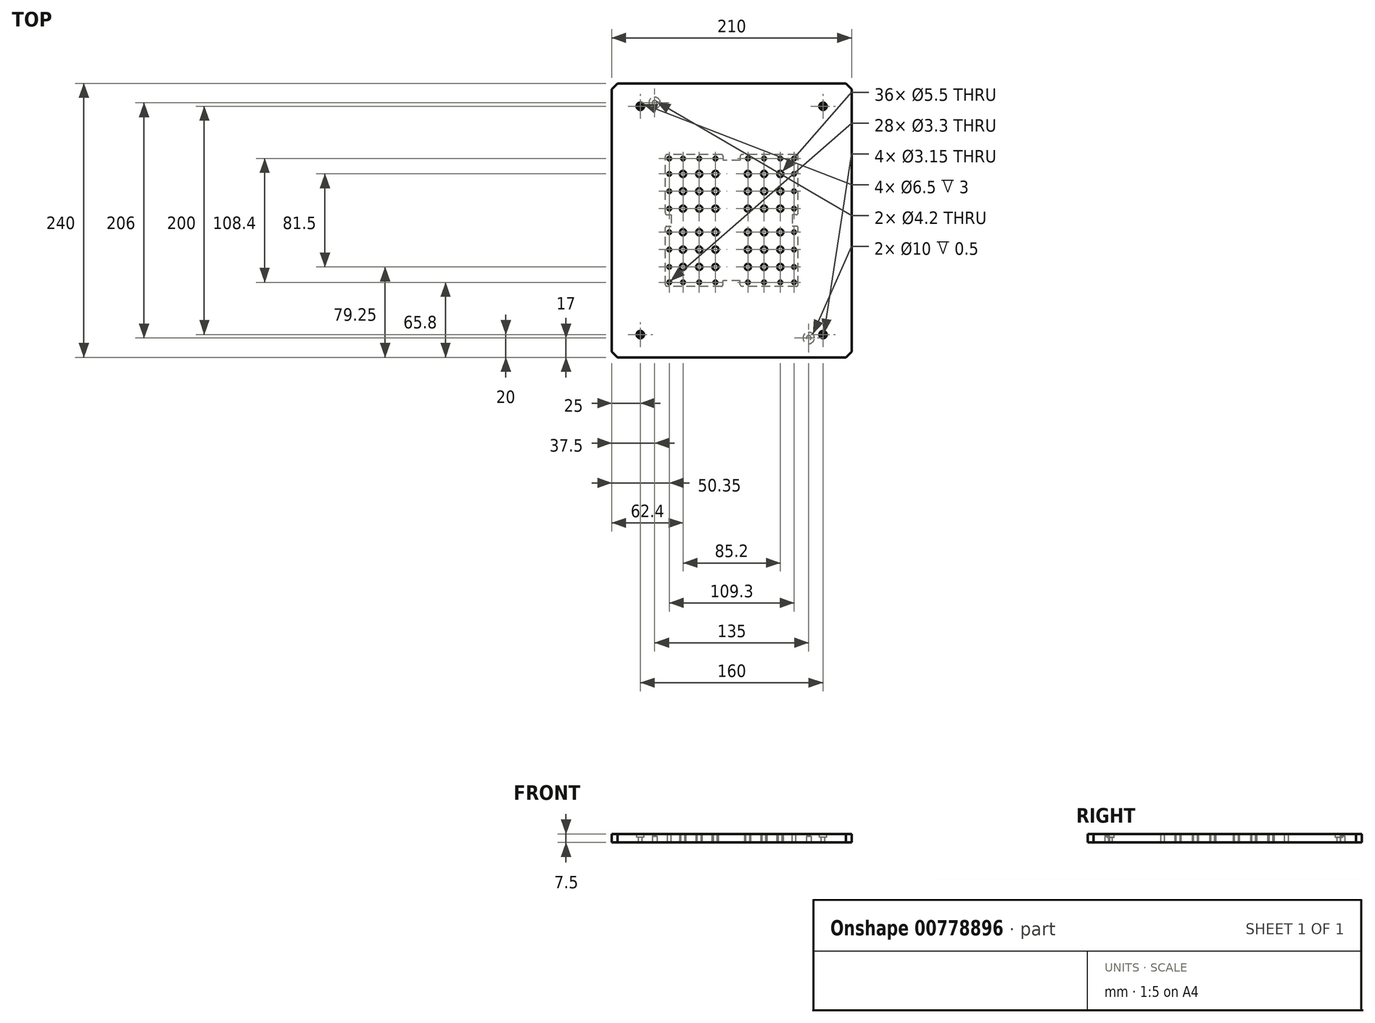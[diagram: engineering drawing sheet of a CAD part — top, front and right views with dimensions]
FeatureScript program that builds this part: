
annotation { "Feature Type Name" : "Feature", "Feature Type Description" : "" }
export const myFeature = defineFeature(function(context is Context, id is Id, definition is map)
    precondition{}
    {
        {
            var Q0;
            Q0=qCreatedBy(makeId("Top.planeOp"),FACE);
            var sketch = newSketch(context, id + "F0", { "sketchPlane" : qUnion([Q0])});
            skLineSegment(sketch, "E0.bottom", {"start": v(105, -120) * mm, "end": v(-105, -120) * mm});
            skLineSegment(sketch, "E0.top", {"start": v(105, 120) * mm, "end": v(-105, 120) * mm});
            skLineSegment(sketch, "E0.left", {"start": v(105, -120) * mm, "end": v(105, 120) * mm});
            skLineSegment(sketch, "E0.right", {"start": v(-105, -120) * mm, "end": v(-105, 120) * mm});
            skPoint(sketch, "E0.middle", {"position": v(0, 0) * mm});
            skSolve(sketch);
        }
        {
            var Q0;
            Q0=qSketchRegion(id+"F0",true);
            extrude(context, id + "F1", {"entities" : qUnion([Q0]), "depth" : 7.5 * mm, "offsetDistance" : 25 * mm});
        }
        {
            var Q0;
            {var subQ0=makeQuery(id+"FKgFJWWETvZhy53_1.opExtrude","SWEPT_FACE",FACE,{"disambiguationData":[OSD([sQuery(id+"FgUPbNIBFcRMYxX_1.wireOp",EDGE,"ntR1g29c-uGG6-7fEA-uUQg-DxyObd0NLvpv.bottom")])]});Q0=makeQuery(id+"FXz76x3AiJeIWhb_1.boolean.opBoolean","SPLIT",FACE,{"disambiguationData":[TD([makeQuery(id+"FKgFJWWETvZhy53_1.boolean.opBoolean","COPY",FACE,{"derivedFrom":subQ0})])],"derivedFrom":makeQuery(id+"FKgFJWWETvZhy53_1.boolean.opBoolean","SPLIT",FACE,{"disambiguationData":[TD([subQ0])],"derivedFrom":makeQuery(id+"F7i0cJTQuz7USHp_1.boolean.opBoolean","SPLIT",FACE,{"disambiguationData":[TD([makeQuery(id+"F7i0cJTQuz7USHp_1.opExtrude","SWEPT_FACE",FACE,{"disambiguationData":[OSD([sQuery(id+"F9ToSxTWYH5D263_1.wireOp",EDGE,"f3O45OLR-dcF2-uwor-dRmz-jWqC6Y4i4P3D.bottom")])]})])],"derivedFrom":makeQuery(id+"F1.opExtrude","CAP_FACE",FACE,{"disambiguationData":[OSD([sQuery(id+"F0.wireOp",EDGE,"E0.bottom"),sQuery(id+"F0.wireOp",EDGE,"E0.top"),sQuery(id+"F0.wireOp",EDGE,"E0.left"),sQuery(id+"F0.wireOp",EDGE,"E0.right")])],"isStart":false})})})});}
            var sketch = newSketch(context, id + "F2", { "sketchPlane" : qUnion([Q0])});
            skLineSegment(sketch, "E1.bottom", {"start": v(80, -100) * mm, "end": v(-80, -100) * mm, "construction": true});
            skLineSegment(sketch, "E1.top", {"start": v(80, 100) * mm, "end": v(-80, 100) * mm, "construction": true});
            skLineSegment(sketch, "E1.left", {"start": v(80, -100) * mm, "end": v(80, 100) * mm, "construction": true});
            skLineSegment(sketch, "E1.right", {"start": v(-80, -100) * mm, "end": v(-80, 100) * mm, "construction": true});
            skPoint(sketch, "E2.middle", {"position": v(0, 0) * mm});
            skSolve(sketch);
        }
        {
            var Q0;
            Q0=sQuery(id+"F2.wireOp",VERTEX,"E1.top.end");
            var Q1;
            Q1=sQuery(id+"F2.wireOp",VERTEX,"E1.top.start");
            var Q2;
            Q2=sQuery(id+"F2.wireOp",VERTEX,"E1.bottom.end");
            var Q3;
            Q3=sQuery(id+"F2.wireOp",VERTEX,"E1.bottom.start");
            var Q4;
            Q4=makeQuery(id+"F1.opExtrude","SWEPT_BODY",BODY,{"disambiguationData":[OSD([sQuery(id+"F0.wireOp",EDGE,"E0.bottom"),sQuery(id+"F0.wireOp",EDGE,"E0.top"),sQuery(id+"F0.wireOp",EDGE,"E0.left"),sQuery(id+"F0.wireOp",EDGE,"E0.right")])]});
            hole(context, id + "F3", {"style" : HoleStyle.C_BORE, "endStyle" : HoleEndStyle.THROUGH, "standardTappedOrClearance" : lookupTablePath({ "standard" : "ISO", "fit" : "Close", "size" : "M3", "type" : "Clearance" }), "standardBlindInLast" : lookupTablePath({ "fit" : "Close", "standard" : "ISO", "size" : "M3", "type" : "Clearance" }), "holeDiameter" : 3.15 * mm, "cBoreDiameter" : 6.5 * mm, "cBoreDepth" : 3 * mm, "majorDiameter" : 3 * mm, "isTappedThrough" : true, "tappedDepth" : 6.5 * mm, "tapClearance" : 3, "locations" : qUnion([Q0, Q1, Q2, Q3]), "scope" : qUnion([Q4])});
        }
        {
            var Q0;
            Q0=makeQuery(id+"F1.opExtrude","CAP_FACE",FACE,{"disambiguationData":[OSD([sQuery(id+"F0.wireOp",EDGE,"E0.bottom"),sQuery(id+"F0.wireOp",EDGE,"E0.top"),sQuery(id+"F0.wireOp",EDGE,"E0.left"),sQuery(id+"F0.wireOp",EDGE,"E0.right")])],"isStart":true});
            var sketch = newSketch(context, id + "F4", { "sketchPlane" : qUnion([Q0])});
            skLineSegment(sketch, "E3.bottom", {"start": v(-67.5, 103) * mm, "end": v(67.5, 103) * mm});
            skLineSegment(sketch, "E3.top", {"start": v(-67.5, -103) * mm, "end": v(67.5, -103) * mm});
            skLineSegment(sketch, "E3.left", {"start": v(-67.5, 103) * mm, "end": v(-67.5, -103) * mm});
            skLineSegment(sketch, "E3.right", {"start": v(67.5, 103) * mm, "end": v(67.5, -103) * mm});
            skPoint(sketch, "E3.middle", {"position": v(0, 0) * mm});
            skSolve(sketch);
        }
        {
            var Q0;
            Q0=sQuery(id+"F4.wireOp",VERTEX,"E3.top.start");
            var Q1;
            Q1=sQuery(id+"F4.wireOp",VERTEX,"E3.bottom.end");
            var Q2;
            Q2=makeQuery(id+"F1.opExtrude","SWEPT_BODY",BODY,{"disambiguationData":[OSD([sQuery(id+"F0.wireOp",EDGE,"E0.bottom"),sQuery(id+"F0.wireOp",EDGE,"E0.top"),sQuery(id+"F0.wireOp",EDGE,"E0.left"),sQuery(id+"F0.wireOp",EDGE,"E0.right")])]});
            hole(context, id + "F5", {"style" : HoleStyle.C_BORE, "endStyle" : HoleEndStyle.BLIND, "holeDiameter" : 4.2 * mm, "cBoreDiameter" : 10 * mm, "cBoreDepth" : 0.5 * mm, "majorDiameter" : 5 * mm, "holeDepth" : 5.5 * mm, "isTappedThrough" : true, "tappedDepth" : 6.5 * mm, "tapClearance" : 3, "locations" : qUnion([Q0, Q1]), "scope" : qUnion([Q2])});
        }
        {
            var Q0;
            Q0=makeQuery(id+"F1.opExtrude","CAP_FACE",FACE,{"disambiguationData":[OSD([sQuery(id+"F0.wireOp",EDGE,"E0.bottom"),sQuery(id+"F0.wireOp",EDGE,"E0.top"),sQuery(id+"F0.wireOp",EDGE,"E0.left"),sQuery(id+"F0.wireOp",EDGE,"E0.right")])],"isStart":false});
            var sketch = newSketch(context, id + "F6", { "sketchPlane" : qUnion([Q0])});
            skPoint(sketch, "E4", {"position": v(-42.6, 40.75) * mm});
            skPoint(sketch, "E5.0.1.0", {"position": v(-42.6, 25.55) * mm});
            skPoint(sketch, "E5.0.2.0", {"position": v(-42.6, 10.35) * mm});
            skPoint(sketch, "E5.1.0.0", {"position": v(-28.4, 40.75) * mm});
            skPoint(sketch, "E5.1.1.0", {"position": v(-28.4, 25.55) * mm});
            skPoint(sketch, "E5.1.2.0", {"position": v(-28.4, 10.35) * mm});
            skPoint(sketch, "E5.2.0.0", {"position": v(-14.2, 40.75) * mm});
            skPoint(sketch, "E5.2.1.0", {"position": v(-14.2, 25.55) * mm});
            skPoint(sketch, "E5.2.2.0", {"position": v(-14.2, 10.35) * mm});
            skPoint(sketch, "E5.3.0.0", {"position": v(0, 40.75) * mm});
            skPoint(sketch, "E5.3.1.0", {"position": v(0, 25.55) * mm});
            skPoint(sketch, "E5.3.2.0", {"position": v(0, 10.35) * mm});
            skPoint(sketch, "E5.4.0.0", {"position": v(14.2, 40.75) * mm});
            skPoint(sketch, "E5.4.1.0", {"position": v(14.2, 25.55) * mm});
            skPoint(sketch, "E5.4.2.0", {"position": v(14.2, 10.35) * mm});
            skPoint(sketch, "E5.5.0.0", {"position": v(28.4, 40.75) * mm});
            skPoint(sketch, "E5.5.1.0", {"position": v(28.4, 25.55) * mm});
            skPoint(sketch, "E5.5.2.0", {"position": v(28.4, 10.35) * mm});
            skPoint(sketch, "E5.6.0.0", {"position": v(42.6, 40.75) * mm});
            skPoint(sketch, "E5.6.1.0", {"position": v(42.6, 25.55) * mm});
            skPoint(sketch, "E5.6.2.0", {"position": v(42.6, 10.35) * mm});
            skLineSegment(sketch, "E5.direction1", {"start": v(-42.6, 40.75) * mm, "end": v(-28.4, 40.75) * mm, "construction": true});
            skLineSegment(sketch, "E5.direction2", {"start": v(-42.6, 40.75) * mm, "end": v(-42.6, 25.55) * mm, "construction": true});
            skLineSegment(sketch, "E6", {"start": v(0, 120) * mm, "end": v(0, -120) * mm, "construction": true});
            skLineSegment(sketch, "E7", {"start": v(-105, 0) * mm, "end": v(105, 0) * mm, "construction": true});
            skPoint(sketch, "E8.MirrorP", {"position": v(0, -40.75) * mm});
            skPoint(sketch, "E9.MirrorP", {"position": v(-42.6, -25.55) * mm});
            skLineSegment(sketch, "E10.MirrorCS", {"start": v(-42.6, -40.75) * mm, "end": v(-42.6, -25.55) * mm, "construction": true});
            skLineSegment(sketch, "E11.MirrorCS", {"start": v(-42.6, -40.75) * mm, "end": v(-28.4, -40.75) * mm, "construction": true});
            skPoint(sketch, "E12.MirrorP", {"position": v(-42.6, -10.35) * mm});
            skPoint(sketch, "E13.MirrorP", {"position": v(0, -25.55) * mm});
            skPoint(sketch, "E14.MirrorP", {"position": v(-28.4, -40.75) * mm});
            skPoint(sketch, "E15.MirrorP", {"position": v(28.4, -25.55) * mm});
            skPoint(sketch, "E16.MirrorP", {"position": v(28.4, -10.35) * mm});
            skPoint(sketch, "E17.MirrorP", {"position": v(-14.2, -25.55) * mm});
            skPoint(sketch, "E18.MirrorP", {"position": v(-42.6, -40.75) * mm});
            skPoint(sketch, "E19.MirrorP", {"position": v(14.2, -25.55) * mm});
            skPoint(sketch, "E20.MirrorP", {"position": v(28.4, -40.75) * mm});
            skPoint(sketch, "E21.MirrorP", {"position": v(-14.2, -40.75) * mm});
            skPoint(sketch, "E22.MirrorP", {"position": v(14.2, -10.35) * mm});
            skPoint(sketch, "E23.MirrorP", {"position": v(-14.2, -10.35) * mm});
            skPoint(sketch, "E24.MirrorP", {"position": v(42.6, -10.35) * mm});
            skPoint(sketch, "E25.MirrorP", {"position": v(0, -10.35) * mm});
            skPoint(sketch, "E26.MirrorP", {"position": v(14.2, -40.75) * mm});
            skPoint(sketch, "E27.MirrorP", {"position": v(42.6, -25.55) * mm});
            skPoint(sketch, "E28.MirrorP", {"position": v(-28.4, -10.35) * mm});
            skPoint(sketch, "E29.MirrorP", {"position": v(-28.4, -25.55) * mm});
            skPoint(sketch, "E30.MirrorP", {"position": v(42.6, -40.75) * mm});
            skLineSegment(sketch, "E31.bottom", {"start": v(58.12, -57.7) * mm, "end": v(-58.13, -57.7) * mm, "construction": true});
            skLineSegment(sketch, "E31.top", {"start": v(58.12, 57.7) * mm, "end": v(-58.12, 57.7) * mm, "construction": true});
            skLineSegment(sketch, "E31.left", {"start": v(58.12, -57.7) * mm, "end": v(58.12, 57.7) * mm, "construction": true});
            skLineSegment(sketch, "E31.right", {"start": v(-58.13, -57.7) * mm, "end": v(-58.12, 57.7) * mm, "construction": true});
            skPoint(sketch, "E31.middle", {"position": v(0, 0) * mm});
            skSolve(sketch);
        }
        {
            var Q0;
            Q0=sQuery(id+"F6.wireOp",VERTEX,"E4");
            var Q1;
            Q1=sQuery(id+"F6.wireOp",VERTEX,"E5.1.0.0");
            var Q2;
            Q2=sQuery(id+"F6.wireOp",VERTEX,"E5.2.0.0");
            var Q3;
            Q3=sQuery(id+"F6.wireOp",VERTEX,"E5.4.0.0");
            var Q4;
            Q4=sQuery(id+"F6.wireOp",VERTEX,"E5.5.0.0");
            var Q5;
            Q5=sQuery(id+"F6.wireOp",VERTEX,"E5.6.0.0");
            var Q6;
            Q6=sQuery(id+"F6.wireOp",VERTEX,"E5.0.1.0");
            var Q7;
            Q7=sQuery(id+"F6.wireOp",VERTEX,"E5.1.1.0");
            var Q8;
            Q8=sQuery(id+"F6.wireOp",VERTEX,"E5.2.1.0");
            var Q9;
            Q9=sQuery(id+"F6.wireOp",VERTEX,"E5.4.1.0");
            var Q10;
            Q10=sQuery(id+"F6.wireOp",VERTEX,"E5.5.1.0");
            var Q11;
            Q11=sQuery(id+"F6.wireOp",VERTEX,"E5.6.1.0");
            var Q12;
            Q12=sQuery(id+"F6.wireOp",VERTEX,"E5.6.2.0");
            var Q13;
            Q13=sQuery(id+"F6.wireOp",VERTEX,"E5.5.2.0");
            var Q14;
            Q14=sQuery(id+"F6.wireOp",VERTEX,"E5.4.2.0");
            var Q15;
            Q15=sQuery(id+"F6.wireOp",VERTEX,"E5.2.2.0");
            var Q16;
            Q16=sQuery(id+"F6.wireOp",VERTEX,"E5.1.2.0");
            var Q17;
            Q17=sQuery(id+"F6.wireOp",VERTEX,"E5.0.2.0");
            var Q18;
            Q18=sQuery(id+"F6.wireOp",VERTEX,"E12.MirrorP");
            var Q19;
            Q19=sQuery(id+"F6.wireOp",VERTEX,"E28.MirrorP");
            var Q20;
            Q20=sQuery(id+"F6.wireOp",VERTEX,"E23.MirrorP");
            var Q21;
            Q21=sQuery(id+"F6.wireOp",VERTEX,"E22.MirrorP");
            var Q22;
            Q22=sQuery(id+"F6.wireOp",VERTEX,"E16.MirrorP");
            var Q23;
            Q23=sQuery(id+"F6.wireOp",VERTEX,"E24.MirrorP");
            var Q24;
            Q24=sQuery(id+"F6.wireOp",VERTEX,"E27.MirrorP");
            var Q25;
            Q25=sQuery(id+"F6.wireOp",VERTEX,"E15.MirrorP");
            var Q26;
            Q26=sQuery(id+"F6.wireOp",VERTEX,"E19.MirrorP");
            var Q27;
            Q27=sQuery(id+"F6.wireOp",VERTEX,"E17.MirrorP");
            var Q28;
            Q28=sQuery(id+"F6.wireOp",VERTEX,"E29.MirrorP");
            var Q29;
            Q29=sQuery(id+"F6.wireOp",VERTEX,"E9.MirrorP");
            var Q30;
            Q30=sQuery(id+"F6.wireOp",VERTEX,"E18.MirrorP");
            var Q31;
            Q31=sQuery(id+"F6.wireOp",VERTEX,"E11.MirrorCS.end");
            var Q32;
            Q32=sQuery(id+"F6.wireOp",VERTEX,"E21.MirrorP");
            var Q33;
            Q33=sQuery(id+"F6.wireOp",VERTEX,"E26.MirrorP");
            var Q34;
            Q34=sQuery(id+"F6.wireOp",VERTEX,"E20.MirrorP");
            var Q35;
            Q35=sQuery(id+"F6.wireOp",VERTEX,"E30.MirrorP");
            var Q36;
            Q36=makeQuery(id+"F1.opExtrude","SWEPT_BODY",BODY,{"disambiguationData":[OSD([sQuery(id+"F0.wireOp",EDGE,"E0.bottom"),sQuery(id+"F0.wireOp",EDGE,"E0.top"),sQuery(id+"F0.wireOp",EDGE,"E0.left"),sQuery(id+"F0.wireOp",EDGE,"E0.right")])]});
            hole(context, id + "F7", {"style" : HoleStyle.SIMPLE, "endStyle" : HoleEndStyle.THROUGH, "standardTappedOrClearance" : lookupTablePath({ "standard" : "ISO", "fit" : "Normal", "size" : "M5", "type" : "Clearance" }), "standardBlindInLast" : lookupTablePath({ "fit" : "Standard", "standard" : "ISO", "size" : "M5", "type" : "Clearance" }), "holeDiameter" : 5.5 * mm, "majorDiameter" : 5 * mm, "isTappedThrough" : true, "tappedDepth" : 6.5 * mm, "tapClearance" : 3, "locations" : qUnion([Q0, Q1, Q2, Q3, Q4, Q5, Q6, Q7, Q8, Q9, Q10, Q11, Q12, Q13, Q14, Q15, Q16, Q17, Q18, Q19, Q20, Q21, Q22, Q23, Q24, Q25, Q26, Q27, Q28, Q29, Q30, Q31, Q32, Q33, Q34, Q35]), "scope" : qUnion([Q36])});
        }
        {
            var Q0;
            Q0=makeQuery(id+"F1.opExtrude","CAP_FACE",FACE,{"disambiguationData":[OSD([sQuery(id+"F0.wireOp",EDGE,"E0.bottom"),sQuery(id+"F0.wireOp",EDGE,"E0.top"),sQuery(id+"F0.wireOp",EDGE,"E0.left"),sQuery(id+"F0.wireOp",EDGE,"E0.right")])],"isStart":false});
            var sketch = newSketch(context, id + "F8", { "sketchPlane" : qUnion([Q0])});
            skLineSegment(sketch, "E32", {"start": v(-105, 0) * mm, "end": v(105, 0) * mm, "construction": true});
            skLineSegment(sketch, "E33", {"start": v(0, 120) * mm, "end": v(0, -120) * mm, "construction": true});
            skPoint(sketch, "E34", {"position": v(-54.65, 40.75) * mm});
            skPoint(sketch, "E35", {"position": v(-54.65, 25.55) * mm});
            skPoint(sketch, "E36", {"position": v(-54.65, 10.35) * mm});
            skPoint(sketch, "E37", {"position": v(-54.65, 54.2) * mm});
            skPoint(sketch, "E38", {"position": v(-42.6, 54.2) * mm});
            skPoint(sketch, "E39", {"position": v(-28.4, 54.2) * mm});
            skPoint(sketch, "E40", {"position": v(-14.2, 54.2) * mm});
            skPoint(sketch, "E41", {"position": v(0, 54.2) * mm});
            skPoint(sketch, "E42", {"position": v(14.2, 54.2) * mm});
            skPoint(sketch, "E43", {"position": v(28.4, 54.2) * mm});
            skPoint(sketch, "E44", {"position": v(42.6, 54.2) * mm});
            skPoint(sketch, "E45", {"position": v(54.65, 54.2) * mm});
            skPoint(sketch, "E46", {"position": v(54.65, 40.75) * mm});
            skPoint(sketch, "E47", {"position": v(54.65, 25.55) * mm});
            skPoint(sketch, "E48", {"position": v(54.65, 10.35) * mm});
            skLineSegment(sketch, "E49", {"start": v(-54.65, 54.2) * mm, "end": v(-42.6, 54.2) * mm, "construction": true});
            skLineSegment(sketch, "E50", {"start": v(42.6, 54.2) * mm, "end": v(54.65, 54.2) * mm, "construction": true});
            skPoint(sketch, "E51.MirrorP", {"position": v(54.65, -10.35) * mm});
            skPoint(sketch, "E52.MirrorP", {"position": v(54.65, -40.75) * mm});
            skPoint(sketch, "E53.MirrorP", {"position": v(54.65, -25.55) * mm});
            skPoint(sketch, "E54.MirrorP", {"position": v(-54.65, -10.35) * mm});
            skPoint(sketch, "E55.MirrorP", {"position": v(-54.65, -25.55) * mm});
            skPoint(sketch, "E56.MirrorP", {"position": v(-54.65, -40.75) * mm});
            skPoint(sketch, "E57.MirrorP", {"position": v(28.4, -54.2) * mm});
            skPoint(sketch, "E58.MirrorP", {"position": v(0, -54.2) * mm});
            skPoint(sketch, "E59.MirrorP", {"position": v(14.2, -54.2) * mm});
            skPoint(sketch, "E60.MirrorP", {"position": v(-14.2, -54.2) * mm});
            skPoint(sketch, "E61.MirrorP", {"position": v(-54.65, -54.2) * mm});
            skPoint(sketch, "E62.MirrorP", {"position": v(-42.6, -54.2) * mm});
            skPoint(sketch, "E63.MirrorP", {"position": v(-28.4, -54.2) * mm});
            skPoint(sketch, "E64.MirrorP", {"position": v(42.6, -54.2) * mm});
            skPoint(sketch, "E65.MirrorP", {"position": v(54.65, -54.2) * mm});
            skSolve(sketch);
        }
        {
            var Q0;
            Q0=sQuery(id+"F8.wireOp",VERTEX,"E37");
            var Q1;
            Q1=sQuery(id+"F8.wireOp",VERTEX,"E38");
            var Q2;
            Q2=sQuery(id+"F8.wireOp",VERTEX,"E39");
            var Q3;
            Q3=sQuery(id+"F8.wireOp",VERTEX,"E40");
            var Q4;
            Q4=sQuery(id+"F8.wireOp",VERTEX,"E42");
            var Q5;
            Q5=sQuery(id+"F8.wireOp",VERTEX,"E43");
            var Q6;
            Q6=sQuery(id+"F8.wireOp",VERTEX,"E44");
            var Q7;
            Q7=sQuery(id+"F8.wireOp",VERTEX,"E45");
            var Q8;
            Q8=sQuery(id+"F8.wireOp",VERTEX,"E46");
            var Q9;
            Q9=sQuery(id+"F8.wireOp",VERTEX,"E47");
            var Q10;
            Q10=sQuery(id+"F8.wireOp",VERTEX,"E48");
            var Q11;
            Q11=sQuery(id+"F8.wireOp",VERTEX,"E51.MirrorP");
            var Q12;
            Q12=sQuery(id+"F8.wireOp",VERTEX,"E53.MirrorP");
            var Q13;
            Q13=sQuery(id+"F8.wireOp",VERTEX,"E52.MirrorP");
            var Q14;
            Q14=sQuery(id+"F8.wireOp",VERTEX,"E65.MirrorP");
            var Q15;
            Q15=sQuery(id+"F8.wireOp",VERTEX,"E64.MirrorP");
            var Q16;
            Q16=sQuery(id+"F8.wireOp",VERTEX,"E57.MirrorP");
            var Q17;
            Q17=sQuery(id+"F8.wireOp",VERTEX,"E59.MirrorP");
            var Q18;
            Q18=sQuery(id+"F8.wireOp",VERTEX,"E60.MirrorP");
            var Q19;
            Q19=sQuery(id+"F8.wireOp",VERTEX,"E63.MirrorP");
            var Q20;
            Q20=sQuery(id+"F8.wireOp",VERTEX,"E62.MirrorP");
            var Q21;
            Q21=sQuery(id+"F8.wireOp",VERTEX,"E61.MirrorP");
            var Q22;
            Q22=sQuery(id+"F8.wireOp",VERTEX,"E56.MirrorP");
            var Q23;
            Q23=sQuery(id+"F8.wireOp",VERTEX,"E55.MirrorP");
            var Q24;
            Q24=sQuery(id+"F8.wireOp",VERTEX,"E54.MirrorP");
            var Q25;
            Q25=sQuery(id+"F8.wireOp",VERTEX,"E36");
            var Q26;
            Q26=sQuery(id+"F8.wireOp",VERTEX,"E35");
            var Q27;
            Q27=sQuery(id+"F8.wireOp",VERTEX,"E34");
            var Q28;
            Q28=makeQuery(id+"F1.opExtrude","SWEPT_BODY",BODY,{"disambiguationData":[OSD([sQuery(id+"F0.wireOp",EDGE,"E0.bottom"),sQuery(id+"F0.wireOp",EDGE,"E0.top"),sQuery(id+"F0.wireOp",EDGE,"E0.left"),sQuery(id+"F0.wireOp",EDGE,"E0.right")])]});
            hole(context, id + "F9", {"style" : HoleStyle.SIMPLE, "endStyle" : HoleEndStyle.THROUGH, "standardTappedOrClearance" : lookupTablePath({ "standard" : "ISO", "fit" : "Normal", "size" : "M3", "type" : "Clearance" }), "standardBlindInLast" : lookupTablePath({ "fit" : "Standard", "standard" : "ISO", "size" : "M3", "type" : "Clearance" }), "holeDiameter" : 3.3 * mm, "majorDiameter" : 5 * mm, "isTappedThrough" : true, "tappedDepth" : 6.5 * mm, "tapClearance" : 3, "locations" : qUnion([Q0, Q1, Q2, Q3, Q4, Q5, Q6, Q7, Q8, Q9, Q10, Q11, Q12, Q13, Q14, Q15, Q16, Q17, Q18, Q19, Q20, Q21, Q22, Q23, Q24, Q25, Q26, Q27]), "scope" : qUnion([Q28])});
        }
        {
            var Q0;
            Q0=makeQuery(id+"F1.opExtrude","CAP_FACE",FACE,{"disambiguationData":[OSD([sQuery(id+"F0.wireOp",EDGE,"E0.bottom"),sQuery(id+"F0.wireOp",EDGE,"E0.top"),sQuery(id+"F0.wireOp",EDGE,"E0.left"),sQuery(id+"F0.wireOp",EDGE,"E0.right")])],"isStart":true});
            var sketch = newSketch(context, id + "F10", { "sketchPlane" : qUnion([Q0])});
            skLineSegment(sketch, "E66.0", {"start": v(56.62, -57.7) * mm, "end": v(-56.62, -57.7) * mm});
            skLineSegment(sketch, "E66.1", {"start": v(58.12, 56.2) * mm, "end": v(58.12, -56.2) * mm});
            skLineSegment(sketch, "E66.2", {"start": v(56.62, 57.7) * mm, "end": v(-56.63, 57.7) * mm});
            skLineSegment(sketch, "E66.3", {"start": v(-58.13, 56.2) * mm, "end": v(-58.12, -56.2) * mm});
            skPoint(sketch, "E67.visualSharp", {"position": v(58.12, -57.7) * mm});
            skArc(sketch, "E67.filletArc", {"start": v(56.62, -57.7) * mm, "mid": v(57.69, -57.26) * mm, "end": v(58.12, -56.2) * mm});
            skPoint(sketch, "E68.visualSharp", {"position": v(-58.12, -57.7) * mm});
            skArc(sketch, "E68.filletArc", {"start": v(-58.12, -56.2) * mm, "mid": v(-57.69, -57.26) * mm, "end": v(-56.62, -57.7) * mm});
            skPoint(sketch, "E69.visualSharp", {"position": v(-58.13, 57.7) * mm});
            skArc(sketch, "E69.filletArc", {"start": v(-56.63, 57.7) * mm, "mid": v(-57.69, 57.26) * mm, "end": v(-58.13, 56.2) * mm});
            skPoint(sketch, "E70.visualSharp", {"position": v(58.12, 57.7) * mm});
            skArc(sketch, "E70.filletArc", {"start": v(58.12, 56.2) * mm, "mid": v(57.69, 57.26) * mm, "end": v(56.62, 57.7) * mm});
            skLineSegment(sketch, "E71.bottom", {"start": v(7.5, -57.7) * mm, "end": v(-7.5, -57.7) * mm});
            skLineSegment(sketch, "E71.top", {"start": v(7.5, -52.7) * mm, "end": v(-7.5, -52.7) * mm});
            skLineSegment(sketch, "E71.left", {"start": v(7.5, -57.7) * mm, "end": v(7.5, -52.7) * mm});
            skLineSegment(sketch, "E71.right", {"start": v(-7.5, -57.7) * mm, "end": v(-7.5, -52.7) * mm});
            skLineSegment(sketch, "E72", {"start": v(0, -120) * mm, "end": v(0, 120) * mm, "construction": true});
            skLineSegment(sketch, "E73", {"start": v(105, 0) * mm, "end": v(-105, 0) * mm, "construction": true});
            skLineSegment(sketch, "E74.MirrorCS", {"start": v(7.5, 57.7) * mm, "end": v(-7.5, 57.7) * mm});
            skLineSegment(sketch, "E75.MirrorCS", {"start": v(7.5, 52.7) * mm, "end": v(-7.5, 52.7) * mm});
            skLineSegment(sketch, "E76.MirrorCS", {"start": v(7.5, 57.7) * mm, "end": v(7.5, 52.7) * mm});
            skLineSegment(sketch, "E77.MirrorCS", {"start": v(-7.5, 57.7) * mm, "end": v(-7.5, 52.7) * mm});
            skLineSegment(sketch, "E78.bottom", {"start": v(58.12, -5) * mm, "end": v(53.13, -5) * mm});
            skLineSegment(sketch, "E78.top", {"start": v(58.12, 5) * mm, "end": v(53.13, 5) * mm});
            skLineSegment(sketch, "E78.left", {"start": v(58.12, -5) * mm, "end": v(58.12, 5) * mm});
            skLineSegment(sketch, "E78.right", {"start": v(53.13, -5) * mm, "end": v(53.13, 5) * mm});
            skLineSegment(sketch, "E79.MirrorCS", {"start": v(-58.12, -5) * mm, "end": v(-53.13, -5) * mm});
            skLineSegment(sketch, "E80.MirrorCS", {"start": v(-58.12, -5) * mm, "end": v(-58.12, 5) * mm});
            skLineSegment(sketch, "E81.MirrorCS", {"start": v(-53.13, -5) * mm, "end": v(-53.13, 5) * mm});
            skLineSegment(sketch, "E82.MirrorCS", {"start": v(-58.12, 5) * mm, "end": v(-53.13, 5) * mm});
            skSolve(sketch);
        }
        {
            var Q0;
            Q0=makeQuery(id+"F10.imprint","IMPRINT",FACE,{"disambiguationData":[TD([[makeQuery(id+"F10.imprint","IMPRINT",EDGE,{"derivedFrom":sQuery(id+"F10.wireOp",EDGE,"E66.1")}),-1.0]])]});
            extrude(context, id + "F11", {"entities" : qUnion([Q0]), "operationType" : NewBodyOperationType.REMOVE, "oppositeDirection" : true, "depth" : 0.5 * mm, "offsetDistance" : 25 * mm});
        }
        {
            var Q0;
            Q0=makeQuery(id+"F1.opExtrude","SWEPT_EDGE",EDGE,{"disambiguationData":[OSD([sQuery(id+"F0.wireOp",EDGE,"E0.top"),sQuery(id+"F0.wireOp",EDGE,"E0.right")])]});
            var Q1;
            Q1=makeQuery(id+"F1.opExtrude","SWEPT_EDGE",EDGE,{"disambiguationData":[OSD([sQuery(id+"F0.wireOp",EDGE,"E0.top"),sQuery(id+"F0.wireOp",EDGE,"E0.left")])]});
            var Q2;
            Q2=makeQuery(id+"F1.opExtrude","SWEPT_EDGE",EDGE,{"disambiguationData":[OSD([sQuery(id+"F0.wireOp",EDGE,"E0.bottom"),sQuery(id+"F0.wireOp",EDGE,"E0.right")])]});
            var Q3;
            Q3=makeQuery(id+"F1.opExtrude","SWEPT_EDGE",EDGE,{"disambiguationData":[OSD([sQuery(id+"F0.wireOp",EDGE,"E0.bottom"),sQuery(id+"F0.wireOp",EDGE,"E0.left")])]});
            chamfer(context, id + "F12", {"entities" : qUnion([Q0, Q1, Q2, Q3]), "width" : 5 * mm, "tangentPropagation" : true});
        }
        {
            var Q0;
            Q0=makeQuery(id+"F11.boolean.opBoolean","COPY",EDGE,{"derivedFrom":makeQuery(id+"F11.opExtrude","SWEPT_EDGE",EDGE,{"disambiguationData":[OSD([sQuery(id+"F10.wireOp",EDGE,"E66.0"),sQuery(id+"F10.wireOp",EDGE,"E71.bottom"),sQuery(id+"F10.wireOp",EDGE,"E71.left")])]})});
            var Q1;
            Q1=makeQuery(id+"F11.boolean.opBoolean","COPY",EDGE,{"derivedFrom":makeQuery(id+"F11.opExtrude","SWEPT_EDGE",EDGE,{"disambiguationData":[OSD([sQuery(id+"F10.wireOp",EDGE,"E66.0"),sQuery(id+"F10.wireOp",EDGE,"E71.bottom"),sQuery(id+"F10.wireOp",EDGE,"E71.right")])]})});
            var Q2;
            Q2=makeQuery(id+"F11.boolean.opBoolean","COPY",EDGE,{"derivedFrom":makeQuery(id+"F11.opExtrude","SWEPT_EDGE",EDGE,{"disambiguationData":[OSD([sQuery(id+"F10.wireOp",EDGE,"E66.1"),sQuery(id+"F10.wireOp",EDGE,"E78.top"),sQuery(id+"F10.wireOp",EDGE,"E78.left")])]})});
            var Q3;
            Q3=makeQuery(id+"F11.boolean.opBoolean","COPY",EDGE,{"derivedFrom":makeQuery(id+"F11.opExtrude","SWEPT_EDGE",EDGE,{"disambiguationData":[OSD([sQuery(id+"F10.wireOp",EDGE,"E66.1"),sQuery(id+"F10.wireOp",EDGE,"E78.bottom"),sQuery(id+"F10.wireOp",EDGE,"E78.left")])]})});
            var Q4;
            Q4=makeQuery(id+"F11.boolean.opBoolean","COPY",EDGE,{"derivedFrom":makeQuery(id+"F11.opExtrude","SWEPT_EDGE",EDGE,{"disambiguationData":[OSD([sQuery(id+"F10.wireOp",EDGE,"E66.2"),sQuery(id+"F10.wireOp",EDGE,"E74.MirrorCS"),sQuery(id+"F10.wireOp",EDGE,"E76.MirrorCS")])]})});
            var Q5;
            Q5=makeQuery(id+"F11.boolean.opBoolean","COPY",EDGE,{"derivedFrom":makeQuery(id+"F11.opExtrude","SWEPT_EDGE",EDGE,{"disambiguationData":[OSD([sQuery(id+"F10.wireOp",EDGE,"E66.2"),sQuery(id+"F10.wireOp",EDGE,"E74.MirrorCS"),sQuery(id+"F10.wireOp",EDGE,"E77.MirrorCS")])]})});
            var Q6;
            Q6=makeQuery(id+"F11.boolean.opBoolean","COPY",EDGE,{"derivedFrom":makeQuery(id+"F11.opExtrude","SWEPT_EDGE",EDGE,{"disambiguationData":[OSD([sQuery(id+"F10.wireOp",EDGE,"E66.3"),sQuery(id+"F10.wireOp",EDGE,"E80.MirrorCS"),sQuery(id+"F10.wireOp",EDGE,"E82.MirrorCS")])]})});
            var Q7;
            Q7=makeQuery(id+"F11.boolean.opBoolean","COPY",EDGE,{"derivedFrom":makeQuery(id+"F11.opExtrude","SWEPT_EDGE",EDGE,{"disambiguationData":[OSD([sQuery(id+"F10.wireOp",EDGE,"E66.3"),sQuery(id+"F10.wireOp",EDGE,"E79.MirrorCS"),sQuery(id+"F10.wireOp",EDGE,"E80.MirrorCS")])]})});
            fillet(context, id + "F13", {"entities" : qUnion([Q0, Q1, Q2, Q3, Q4, Q5, Q6, Q7]), "radius" : 1.5 * mm, "tangentPropagation" : true, "allowEdgeOverflow" : false});
        }
    });
